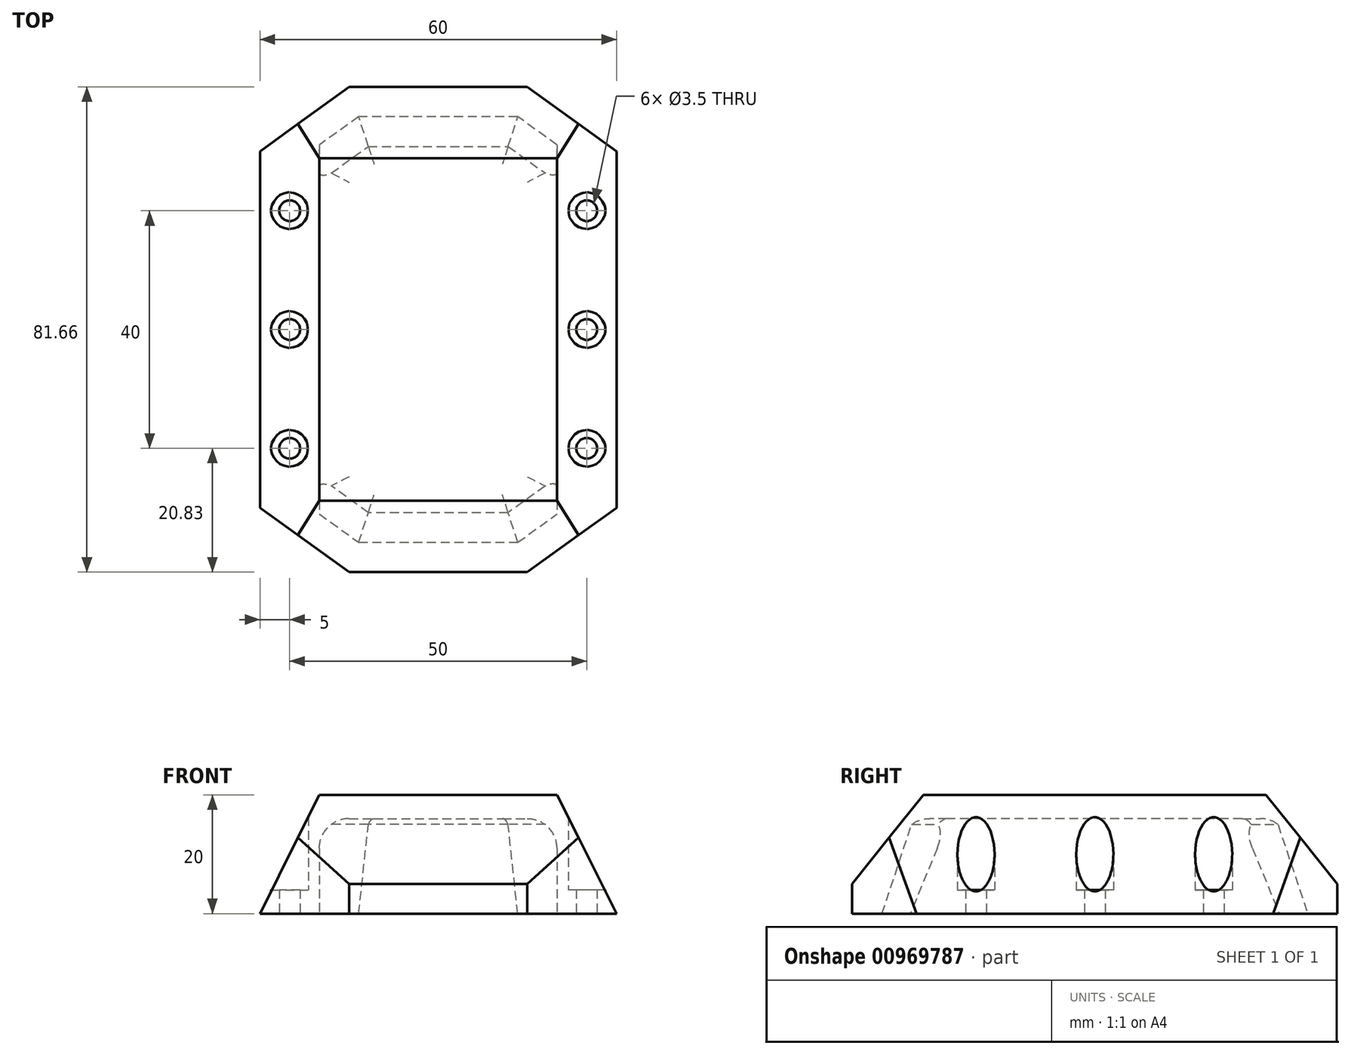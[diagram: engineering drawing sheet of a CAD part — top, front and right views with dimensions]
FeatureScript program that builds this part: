
annotation { "Feature Type Name" : "Feature", "Feature Type Description" : "" }
export const myFeature = defineFeature(function(context is Context, id is Id, definition is map)
    precondition{}
    {
        {
            var Q0;
            Q0=qCreatedBy(makeId("Top.planeOp"),FACE);
            var sketch = newSketch(context, id + "F0", { "sketchPlane" : qUnion([Q0])});
            skCircle(sketch, "E0", {"center": v(-25, 20) * mm, "radius": 1.75 * mm});
            skCircle(sketch, "E1", {"center": v(-25, 0) * mm, "radius": 1.75 * mm});
            skCircle(sketch, "E2", {"center": v(-25, -20) * mm, "radius": 1.75 * mm});
            skCircle(sketch, "E3", {"center": v(25, 20) * mm, "radius": 1.75 * mm});
            skCircle(sketch, "E4", {"center": v(25, 0) * mm, "radius": 1.75 * mm});
            skCircle(sketch, "E5", {"center": v(25, -20) * mm, "radius": 1.75 * mm});
            skLineSegment(sketch, "E6", {"start": v(-25, 0) * mm, "end": v(-25, 20) * mm, "construction": true});
            skLineSegment(sketch, "E7", {"start": v(-25, 0) * mm, "end": v(-25, -20) * mm, "construction": true});
            skLineSegment(sketch, "E8", {"start": v(-30, 30) * mm, "end": v(-30, -30) * mm});
            skPoint(sketch, "E9", {"position": v(-30, 0) * mm});
            skLineSegment(sketch, "E10", {"start": v(-30, 30) * mm, "end": v(-15, 40.83) * mm});
            skLineSegment(sketch, "E11.MirrorCS", {"start": v(-30, -30) * mm, "end": v(-15, -40.83) * mm});
            skLineSegment(sketch, "E12.MirrorCS", {"start": v(30, 30) * mm, "end": v(15, 40.83) * mm});
            skLineSegment(sketch, "E13.MirrorCS", {"start": v(30, 30) * mm, "end": v(30, -30) * mm});
            skLineSegment(sketch, "E14.MirrorCS", {"start": v(30, -30) * mm, "end": v(15, -40.83) * mm});
            skLineSegment(sketch, "E15", {"start": v(-15, 40.83) * mm, "end": v(15, 40.83) * mm});
            skLineSegment(sketch, "E16", {"start": v(-15, -40.83) * mm, "end": v(15, -40.83) * mm});
            skLineSegment(sketch, "E17.0", {"start": v(-20, -24.89) * mm, "end": v(-11.77, -30.83) * mm});
            skLineSegment(sketch, "E17.1", {"start": v(-20, 24.89) * mm, "end": v(-20, -24.89) * mm});
            skLineSegment(sketch, "E17.2", {"start": v(-11.77, -30.83) * mm, "end": v(11.77, -30.83) * mm});
            skLineSegment(sketch, "E17.3", {"start": v(-20, 24.89) * mm, "end": v(-11.77, 30.83) * mm});
            skLineSegment(sketch, "E17.4", {"start": v(20, -24.89) * mm, "end": v(11.77, -30.83) * mm});
            skLineSegment(sketch, "E17.5", {"start": v(20, 24.89) * mm, "end": v(20, -24.89) * mm});
            skLineSegment(sketch, "E17.6", {"start": v(20, 24.89) * mm, "end": v(11.77, 30.83) * mm});
            skLineSegment(sketch, "E17.7", {"start": v(-11.77, 30.83) * mm, "end": v(11.77, 30.83) * mm});
            skCircle(sketch, "E18", {"center": v(-25, -20) * mm, "radius": 3.12 * mm});
            skCircle(sketch, "E19", {"center": v(-25, 0) * mm, "radius": 3.12 * mm});
            skCircle(sketch, "E20", {"center": v(-25, 20) * mm, "radius": 3.12 * mm});
            skCircle(sketch, "E21.MirrorC", {"center": v(25, 20) * mm, "radius": 3.12 * mm});
            skCircle(sketch, "E22.MirrorC", {"center": v(25, 0) * mm, "radius": 3.12 * mm});
            skCircle(sketch, "E23.MirrorC", {"center": v(25, -20) * mm, "radius": 3.12 * mm});
            skSolve(sketch);
        }
        {
            var Q0;
            Q0=makeQuery(id+"F0.imprint","IMPRINT",FACE,{"disambiguationData":[TD([[makeQuery(id+"F0.imprint","IMPRINT",EDGE,{"derivedFrom":sQuery(id+"F0.wireOp",EDGE,"E8")}),1.0]])]});
            extrude(context, id + "F1", {"entities" : qUnion([Q0]), "depth" : 20 * mm, "offsetDistance" : 25 * mm});
        }
        {
            var Q0;
            Q0=makeQuery(id+"F0.imprint","IMPRINT",FACE,{"disambiguationData":[TD([[makeQuery(id+"F0.imprint","IMPRINT",EDGE,{"derivedFrom":sQuery(id+"F0.wireOp",EDGE,"E17.0")}),1.0]])]});
            extrude(context, id + "F2", {"entities" : qUnion([Q0]), "operationType" : NewBodyOperationType.ADD, "depth" : 20 * mm, "offsetDistance" : 25 * mm, "hasSecondDirection" : true, "secondDirectionOppositeDirection" : false, "secondDirectionDepth" : 16 * mm});
        }
        {
            var Q0;
            Q0=makeQuery(id+"F1.opExtrude","CAP_EDGE",EDGE,{"disambiguationData":[OSD([sQuery(id+"F0.wireOp",EDGE,"E8")])],"isStart":false});
            var Q1;
            Q1=makeQuery(id+"F1.opExtrude","CAP_EDGE",EDGE,{"disambiguationData":[OSD([sQuery(id+"F0.wireOp",EDGE,"E13.MirrorCS")])],"isStart":false});
            chamfer(context, id + "F3", {"entities" : qUnion([Q0, Q1]), "chamferType" : ChamferType.TWO_OFFSETS, "width1" : 10 * mm, "oppositeDirection" : false, "width2" : 20 * mm, "tangentPropagation" : true});
        }
        {
            var Q0;
            Q0=makeQuery(id+"F1.opExtrude","CAP_EDGE",EDGE,{"disambiguationData":[OSD([sQuery(id+"F0.wireOp",EDGE,"E16")])],"isStart":false});
            var Q1;
            Q1=makeQuery(id+"F1.opExtrude","CAP_EDGE",EDGE,{"disambiguationData":[OSD([sQuery(id+"F0.wireOp",EDGE,"E15")])],"isStart":false});
            chamfer(context, id + "F4", {"entities" : qUnion([Q0, Q1]), "chamferType" : ChamferType.TWO_OFFSETS, "width1" : 12 * mm, "oppositeDirection" : false, "width2" : 15 * mm, "tangentPropagation" : true});
        }
        {
            var Q0;
            Q0=makeQuery(id+"F0.imprint","IMPRINT",FACE,{"disambiguationData":[TD([[makeQuery(id+"F0.imprint","IMPRINT",EDGE,{"derivedFrom":sQuery(id+"F0.wireOp",EDGE,"E5")}),-1.0]])]});
            var Q1;
            Q1=makeQuery(id+"F0.imprint","IMPRINT",FACE,{"disambiguationData":[TD([[makeQuery(id+"F0.imprint","IMPRINT",EDGE,{"derivedFrom":sQuery(id+"F0.wireOp",EDGE,"E4")}),-1.0]])]});
            var Q2;
            Q2=makeQuery(id+"F0.imprint","IMPRINT",FACE,{"disambiguationData":[TD([[makeQuery(id+"F0.imprint","IMPRINT",EDGE,{"derivedFrom":sQuery(id+"F0.wireOp",EDGE,"E3")}),-1.0]])]});
            var Q3;
            Q3=makeQuery(id+"F0.imprint","IMPRINT",FACE,{"disambiguationData":[TD([[makeQuery(id+"F0.imprint","IMPRINT",EDGE,{"derivedFrom":sQuery(id+"F0.wireOp",EDGE,"E2")}),-1.0]])]});
            var Q4;
            Q4=makeQuery(id+"F0.imprint","IMPRINT",FACE,{"disambiguationData":[TD([[makeQuery(id+"F0.imprint","IMPRINT",EDGE,{"derivedFrom":sQuery(id+"F0.wireOp",EDGE,"E1")}),-1.0]])]});
            var Q5;
            Q5=makeQuery(id+"F0.imprint","IMPRINT",FACE,{"disambiguationData":[TD([[makeQuery(id+"F0.imprint","IMPRINT",EDGE,{"derivedFrom":sQuery(id+"F0.wireOp",EDGE,"E0")}),-1.0]])]});
            extrude(context, id + "F5", {"entities" : qUnion([Q0, Q1, Q2, Q3, Q4, Q5]), "operationType" : NewBodyOperationType.ADD, "depth" : 4 * mm, "offsetDistance" : 25 * mm});
        }
        {
            var Q0;
            Q0=makeQuery(id+"F1.opExtrude","CAP_EDGE",EDGE,{"disambiguationData":[OSD([sQuery(id+"F0.wireOp",EDGE,"E17.7")])],"isStart":true});
            var Q1;
            Q1=makeQuery(id+"F1.opExtrude","CAP_EDGE",EDGE,{"disambiguationData":[OSD([sQuery(id+"F0.wireOp",EDGE,"E17.3")])],"isStart":true});
            var Q2;
            Q2=makeQuery(id+"F1.opExtrude","CAP_EDGE",EDGE,{"disambiguationData":[OSD([sQuery(id+"F0.wireOp",EDGE,"E17.6")])],"isStart":true});
            var Q3;
            Q3=makeQuery(id+"F1.opExtrude","CAP_EDGE",EDGE,{"disambiguationData":[OSD([sQuery(id+"F0.wireOp",EDGE,"E17.2")])],"isStart":true});
            var Q4;
            Q4=makeQuery(id+"F1.opExtrude","CAP_EDGE",EDGE,{"disambiguationData":[OSD([sQuery(id+"F0.wireOp",EDGE,"E17.0")])],"isStart":true});
            var Q5;
            Q5=makeQuery(id+"F1.opExtrude","CAP_EDGE",EDGE,{"disambiguationData":[OSD([sQuery(id+"F0.wireOp",EDGE,"E17.4")])],"isStart":true});
            chamfer(context, id + "F6", {"entities" : qUnion([Q0, Q1, Q2, Q3, Q4, Q5]), "chamferType" : ChamferType.TWO_OFFSETS, "width1" : 15 * mm, "oppositeDirection" : false, "width2" : 5 * mm, "tangentPropagation" : true});
        }
        {
            var Q0;
            Q0=makeQuery(id+"F2.opExtrude","CAP_FACE",FACE,{"disambiguationData":[OSD([sQuery(id+"F0.wireOp",EDGE,"E17.0"),sQuery(id+"F0.wireOp",EDGE,"E17.1"),sQuery(id+"F0.wireOp",EDGE,"E17.2"),sQuery(id+"F0.wireOp",EDGE,"E17.3"),sQuery(id+"F0.wireOp",EDGE,"E17.4"),sQuery(id+"F0.wireOp",EDGE,"E17.5"),sQuery(id+"F0.wireOp",EDGE,"E17.6"),sQuery(id+"F0.wireOp",EDGE,"E17.7")])],"isStart":true});
            fillet(context, id + "F7", {"entities" : qUnion([Q0]), "radius" : 5 * mm, "tangentPropagation" : true, "allowEdgeOverflow" : false});
        }
    });
